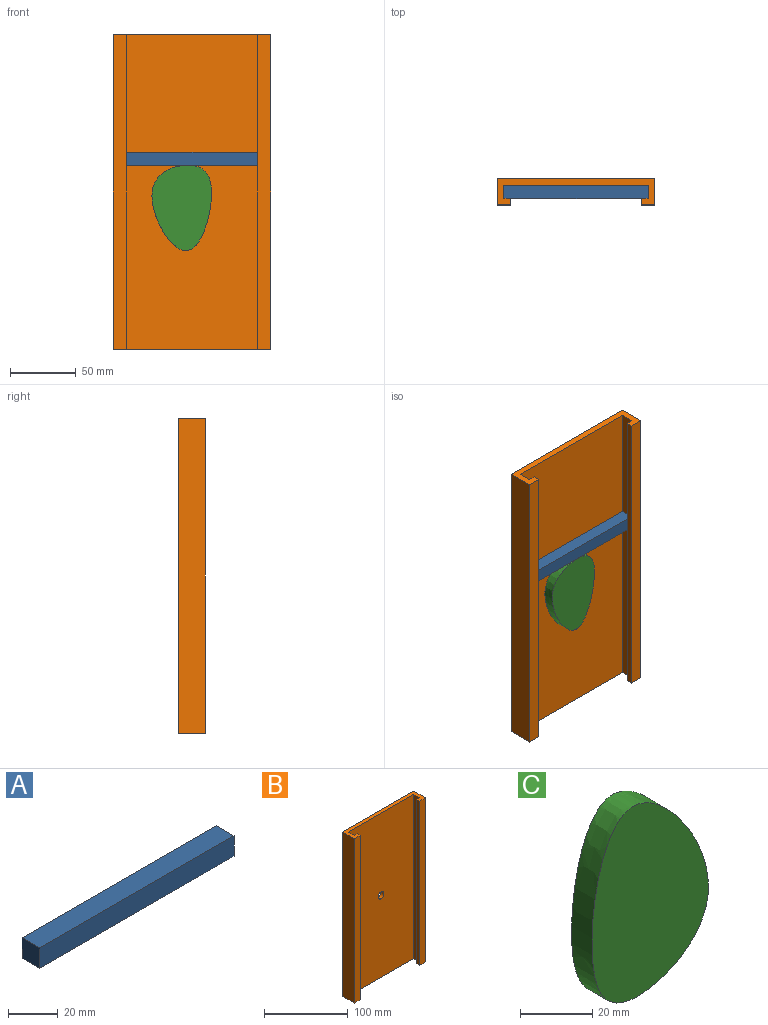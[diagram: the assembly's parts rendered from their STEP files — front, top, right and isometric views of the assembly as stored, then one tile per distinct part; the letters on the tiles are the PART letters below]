
ASSEMBLY  parts=3 mates=2
PART A: 6 faces, bbox 110x10x10 mm
  f0: plane 10x10mm, normal (1,0,0), area 100mm2, adj f1,f2,f4,f5
  f1: plane 110x10mm, normal (0,0,1), area 1100mm2, adj f0,f3,f4,f5
  f2: plane 110x10mm, normal (0,0,-1), area 1100mm2, adj f0,f3,f4,f5
  f3: plane 10x10mm, normal (-1,0,0), area 100mm2, adj f1,f2,f4,f5
  f4: plane 110x10mm, normal (0,1,0), area 1100mm2, adj f0,f1,f2,f3
  f5: plane 110x10mm, normal (0,-1,0), area 1100mm2, adj f0,f1,f2,f3
PART B: 15 faces, bbox 120x20x240 mm
  f0: plane 240x5mm, normal (1,0,0), area 1200mm2, adj f1,f3,f8,f13
  f1: plane 120x20mm, normal (0,0,-1), area 800mm2, adj f0,f2,f4,f5,f6,f7,f8,f9
  f2: plane 240x5mm, normal (-1,0,0), area 1200mm2, adj f1,f3,f6,f11
  f3: plane 120x20mm, normal (0,0,1), area 800mm2, adj f0,f2,f4,f5,f6,f7,f8,f9
  f4: plane 240x110mm, normal (0,-1,0), area 26321.5mm2, adj f1,f3,f5,f7,f14
  f5: plane 240x10mm, normal (-1,0,0), area 2400mm2, adj f1,f3,f4,f6
  f6: plane 240x5mm, normal (0,1,0), area 1200mm2, adj f1,f2,f3,f5
  f7: plane 240x10mm, normal (1,0,0), area 2400mm2, adj f1,f3,f4,f8
  f8: plane 240x5mm, normal (0,1,0), area 1200mm2, adj f0,f1,f3,f7
  f9: plane 240x120mm, normal (0,1,0), area 28721.5mm2, adj f1,f3,f10,f12,f14
  f10: plane 240x20mm, normal (1,0,0), area 4800mm2, adj f1,f3,f9,f11
  f11: plane 240x10mm, normal (0,-1,0), area 2400mm2, adj f1,f2,f3,f10
  f12: plane 240x20mm, normal (-1,0,0), area 4800mm2, adj f1,f3,f9,f13
  f13: plane 240x10mm, normal (0,-1,0), area 2400mm2, adj f0,f1,f3,f12
  f14: cylinder r=5mm len=10mm, axis (0,-1,0), area 157.1mm2, adj f4,f9
PART C: 5 faces, bbox 51x15x69 mm
  f0: plane 10x10mm, normal (0,1,0), area 78.5mm2, adj f1
  f1: cylinder r=5mm len=10mm, axis (0,-1,0), area 219.9mm2, adj f0,f4
  f2: extruded ~65.1x45.46mm, area 1405.8mm2, adj f3,f4
  f3: plane 69.02x51.05mm, normal (0,-1,0), area 2271.9mm2, adj f2
  f4: plane 69.02x51.05mm, normal (0,1,0), area 2193.4mm2, adj f1,f2
PLACE A rot(axis=(0,1,0),0deg) t=(0,0,-89.53)mm
PLACE B at identity fixed
PLACE C rot(axis=(0,-1,0),173.7deg) t=(119.28,0,-13.15)mm
MATE slider B.f3 <-> A.f1  axis (0,0,1) through (-55,2,120)mm
MATE revolute B.f14 <-> C.f1  axis (0,1,0) through (0,7,0)mm
